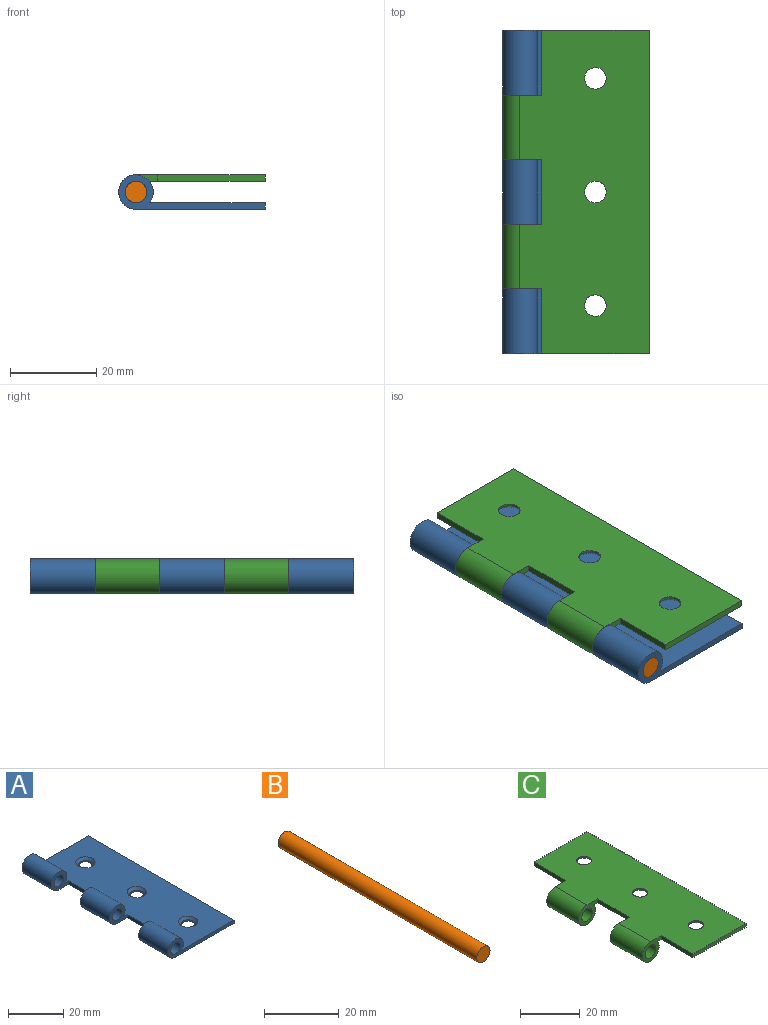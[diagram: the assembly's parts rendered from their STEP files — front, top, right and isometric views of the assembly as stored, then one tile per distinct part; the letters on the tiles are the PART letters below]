
ASSEMBLY  parts=3 mates=2
PART A: 23 faces, bbox 34x75x8 mm
  f0: plane 75x26.88mm, normal (0,0,1), area 1844mm2, adj f1,f2,f3,f4,f5,f6,f7,f8
  f1: plane 15x1.5mm, normal (-1,0,0), area 22.5mm2, adj f0,f2,f12,f13
  f2: plane 9x8mm, normal (0,1,0), area 34.9mm2, adj f0,f1,f13,f18,f19
  f3: plane 34x8mm, normal (0,-1,0), area 72.4mm2, adj f0,f4,f13,f18,f19
  f4: plane 75x1.5mm, normal (1,0,0), area 112.5mm2, adj f0,f3,f5,f13
  f5: plane 34x8mm, normal (0,1,0), area 72.4mm2, adj f0,f4,f13,f14,f15
  f6: plane 9x8mm, normal (0,-1,0), area 34.9mm2, adj f0,f7,f13,f14,f15
  f7: plane 15x1.5mm, normal (-1,0,0), area 22.5mm2, adj f0,f6,f8,f13
  f8: plane 9x8mm, normal (0,1,0), area 34.9mm2, adj f0,f7,f13,f16,f17
  f9: cylinder r=2.5mm len=5mm, axis (0,0,-1), area 7.9mm2, adj f13,f22
  f10: cylinder r=2.5mm len=5mm, axis (0,0,-1), area 7.9mm2, adj f13,f21
  f11: cylinder r=2.5mm len=5mm, axis (0,0,-1), area 7.9mm2, adj f13,f20
  f12: plane 9x8mm, normal (0,-1,0), area 34.9mm2, adj f0,f1,f13,f16,f17
  f13: plane 75x30mm, normal (0,0,-1), area 2041.1mm2, adj f1,f2,f3,f4,f5,f6,f7,f8
  f14: cylinder r=4mm len=15mm, axis (0,1,0), area 323.3mm2, adj f0,f5,f6,f13
  f15: cylinder r=2.5mm len=15mm, axis (0,1,0), area 235.6mm2, adj f5,f6
  f16: cylinder r=4mm len=15mm, axis (0,1,0), area 323.3mm2, adj f0,f8,f12,f13
  f17: cylinder r=2.5mm len=15mm, axis (0,1,0), area 235.6mm2, adj f8,f12
  f18: cylinder r=4mm len=15mm, axis (0,1,0), area 323.3mm2, adj f0,f2,f3,f13
  f19: cylinder r=2.5mm len=15mm, axis (0,1,0), area 235.6mm2, adj f2,f3
  f20: cone r=2.5mm half-angle=45deg, axis (0,0,1), area 26.7mm2, adj f0,f11
  f21: cone r=2.5mm half-angle=45deg, axis (0,0,1), area 26.7mm2, adj f0,f10
  f22: cone r=2.5mm half-angle=45deg, axis (0,0,1), area 26.7mm2, adj f0,f9
PART B: 3 faces, bbox 5x75x5 mm
  f0: plane 5x5mm, normal (0,-1,0), area 19.6mm2, adj f1
  f1: cylinder r=2.5mm len=75mm, axis (0,1,0), area 1178.1mm2, adj f0,f2
  f2: plane 5x5mm, normal (0,1,0), area 19.6mm2, adj f1
PART C: 22 faces, bbox 34x75x8 mm
  f0: plane 75x1.5mm, normal (1,0,0), area 112.5mm2, adj f1,f11,f13,f14
  f1: plane 25x1.5mm, normal (0,1,0), area 37.5mm2, adj f0,f2,f13,f14
  f2: plane 15x1.5mm, normal (-1,0,0), area 22.5mm2, adj f1,f3,f13,f14
  f3: plane 9x8mm, normal (0,1,0), area 34.9mm2, adj f2,f13,f14,f15,f16
  f4: plane 9x8mm, normal (0,-1,0), area 34.9mm2, adj f5,f13,f14,f15,f16
  f5: plane 15x1.5mm, normal (-1,0,0), area 22.5mm2, adj f4,f6,f13,f14
  f6: plane 9x8mm, normal (0,1,0), area 34.9mm2, adj f5,f13,f14,f17,f18
  f7: plane 9x8mm, normal (0,-1,0), area 34.9mm2, adj f8,f13,f14,f17,f18
  f8: plane 15x1.5mm, normal (-1,0,0), area 22.5mm2, adj f7,f11,f13,f14
  f9: cylinder r=2.5mm len=5mm, axis (0,0,1), area 7.9mm2, adj f14,f21
  f10: cylinder r=2.5mm len=5mm, axis (0,0,1), area 7.9mm2, adj f14,f19
  f11: plane 25x1.5mm, normal (0,-1,0), area 37.5mm2, adj f0,f8,f13,f14
  f12: cylinder r=2.5mm len=5mm, axis (0,0,1), area 7.9mm2, adj f14,f20
  f13: plane 75x26.88mm, normal (0,0,-1), area 1815.9mm2, adj f0,f1,f2,f3,f4,f5,f6,f7
  f14: plane 75x30mm, normal (0,0,1), area 1966.1mm2, adj f0,f1,f2,f3,f4,f5,f6,f7
  f15: cylinder r=4mm len=15mm, axis (0,1,0), area 323.3mm2, adj f3,f4,f13,f14
  f16: cylinder r=2.5mm len=15mm, axis (0,1,0), area 235.6mm2, adj f3,f4
  f17: cylinder r=4mm len=15mm, axis (0,1,0), area 323.3mm2, adj f6,f7,f13,f14
  f18: cylinder r=2.5mm len=15mm, axis (0,1,0), area 235.6mm2, adj f6,f7
  f19: cone r=3.5mm half-angle=45deg, axis (0,0,-1), area 26.7mm2, adj f10,f13
  f20: cone r=3.5mm half-angle=45deg, axis (0,0,-1), area 26.7mm2, adj f12,f13
  f21: cone r=3.5mm half-angle=45deg, axis (0,0,-1), area 26.7mm2, adj f9,f13
PLACE A t=(-24.93,0.02,0)mm
PLACE B t=(-24.93,0.02,0)mm
PLACE C t=(-24.93,0.02,0)mm
MATE revolute C.f15 <-> A.f14  axis (0,-1,0) through (-29.93,15.02,4)mm
MATE fastened B.f1 <-> A.f14  axis (0,-1,0) through (-29.93,0.02,4)mm
